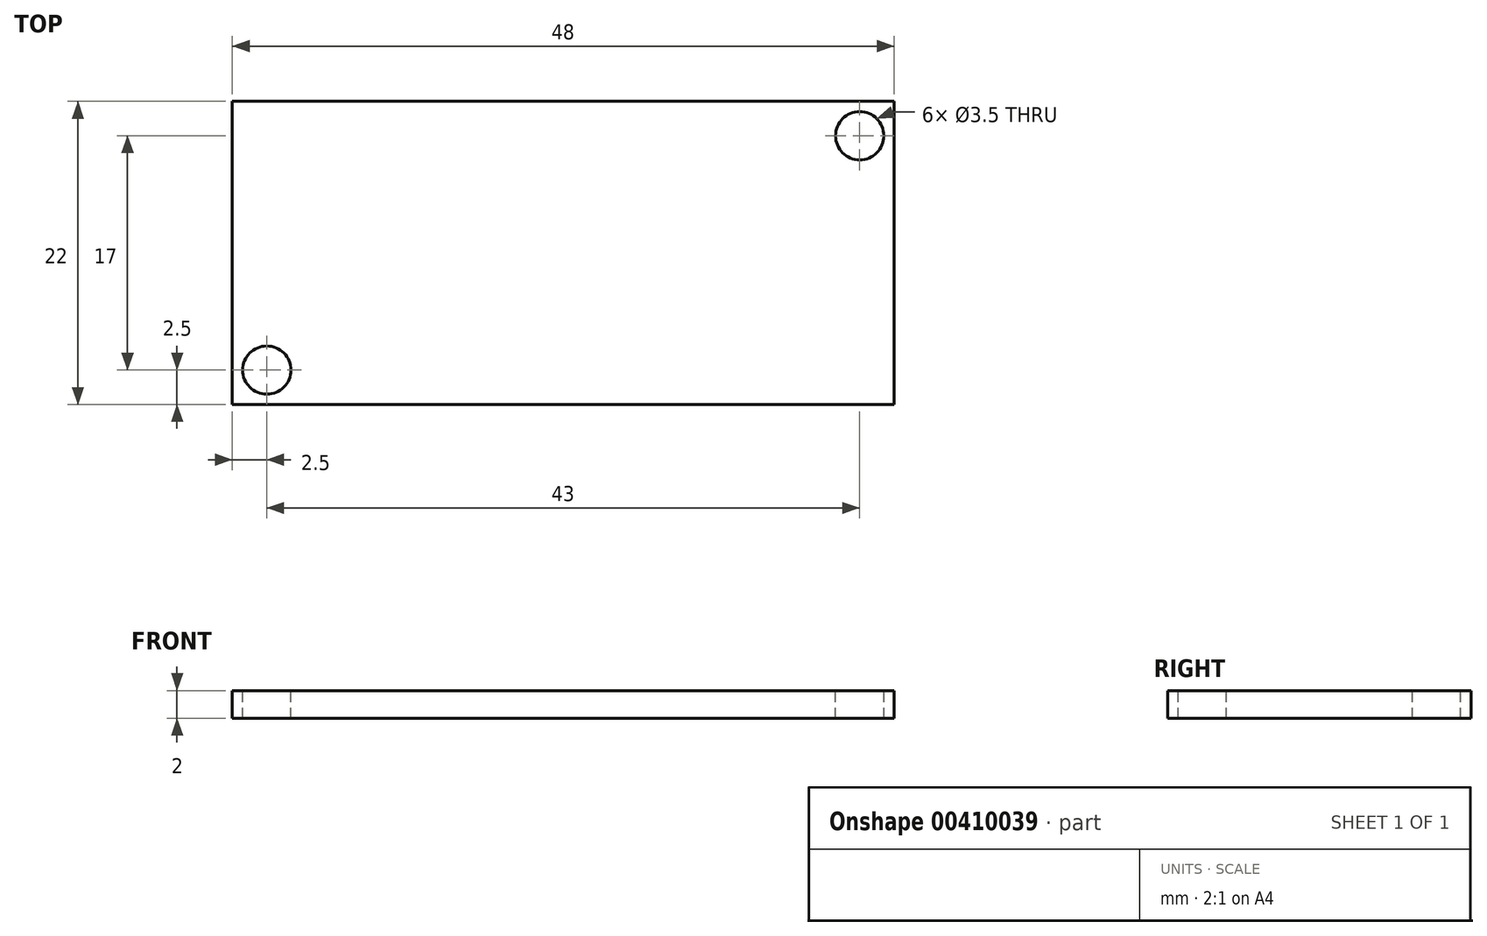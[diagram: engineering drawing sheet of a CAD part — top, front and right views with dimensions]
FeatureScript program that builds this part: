
annotation { "Feature Type Name" : "Feature", "Feature Type Description" : "" }
export const myFeature = defineFeature(function(context is Context, id is Id, definition is map)
    precondition{}
    {
        {
            var Q0;
            Q0=qCreatedBy(makeId("Top.planeOp"),FACE);
            var sketch = newSketch(context, id + "F0", { "sketchPlane" : qUnion([Q0])});
            skLineSegment(sketch, "E0.bottom", {"start": v(0, 0) * mm, "end": v(48, 0) * mm});
            skLineSegment(sketch, "E0.top", {"start": v(0, 22) * mm, "end": v(48, 22) * mm});
            skLineSegment(sketch, "E0.left", {"start": v(0, 0) * mm, "end": v(0, 22) * mm});
            skLineSegment(sketch, "E0.right", {"start": v(48, 0) * mm, "end": v(48, 22) * mm});
            skSolve(sketch);
        }
        {
            var Q0;
            Q0=makeQuery(id+"F0.imprint","IMPRINT",FACE,{"disambiguationData":[TD([[makeQuery(id+"F0.imprint","IMPRINT",EDGE,{"derivedFrom":sQuery(id+"F0.wireOp",EDGE,"E0.bottom")}),1.0]])]});
            extrude(context, id + "F1", {"entities" : qUnion([Q0]), "depth" : 2 * mm});
        }
        {
            var Q0;
            Q0=makeQuery(id+"F1.opExtrude","CAP_FACE",FACE,{"disambiguationData":[OSD([sQuery(id+"F0.wireOp",EDGE,"E0.bottom"),sQuery(id+"F0.wireOp",EDGE,"E0.top"),sQuery(id+"F0.wireOp",EDGE,"E0.left"),sQuery(id+"F0.wireOp",EDGE,"E0.right")])],"isStart":false});
            var sketch = newSketch(context, id + "F2", { "sketchPlane" : qUnion([Q0])});
            skCircle(sketch, "E1", {"center": v(2.5, 2.5) * mm, "radius": 1.75 * mm});
            skCircle(sketch, "E2", {"center": v(45.5, 19.5) * mm, "radius": 1.75 * mm});
            skSolve(sketch);
        }
        {
            var Q0;
            Q0=qSketchRegion(id+"F2",true);
            extrude(context, id + "F3", {"entities" : qUnion([Q0]), "operationType" : NewBodyOperationType.REMOVE, "oppositeDirection" : true, "depth" : 6.74 * mm});
        }
    });
